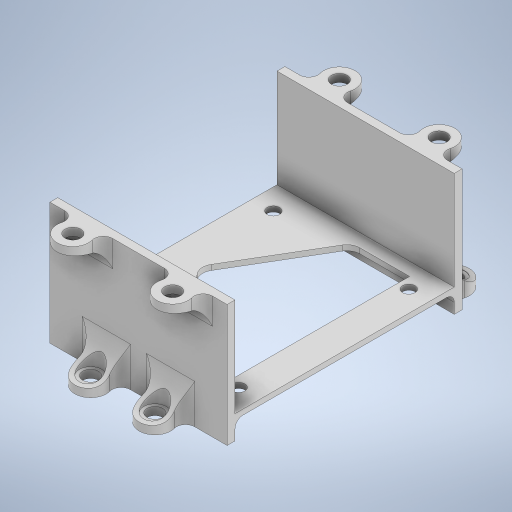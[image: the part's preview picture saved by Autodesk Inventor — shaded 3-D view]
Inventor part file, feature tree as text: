
AUTODESK INVENTOR PART (.ipt)
format: ipt  version: 2024 (Build 280153000, 153)  size: 629,248 bytes
history: native  units: in
note: dims shown in document units (in); Inventor stores cm internally (conversion verified against a paired STEP export)
features: extrude x9, sketch x3, fillet x2, plane x1, projected_geometry x1
ambient origin geometry x8: Origin, YZ Plane, XZ Plane, XY Plane, X Axis, Y Axis, Z Axis, Center Point
bodies: Solid1 (feature_tree)
feature tree (16):
  extrude  "Extrusion1"  Depth=0.1181in
  extrude  "Extrusion2"  Depth=0.1969in
  extrude  "Extrusion6"  Depth=0.4724in
  extrude  "Extrusion7"  Depth=0.4724in
  extrude  "Extrusion8"  Depth=2.6575in
  plane  "Work Plane1"
  extrude  "Extrusion9"  Depth=1.3287in
  fillet  "Fillet2"  Radius=1.6437in
  fillet  "Fillet7"  Radius=0.0787in
  extrude  "Extrusion10"  Depth=1.5551in TaperAngle=0.0deg
  extrude  "Extrusion11"  Depth=0.185in
  extrude  "Extrusion12"  Depth=0.313in
  sketch  "Sketch9"  dims[d0=3.2874in d1=0.1181in]
  sketch  "Sketch10"  dims[d2=0.1181in d4=0.1969in]
  sketch  "Sketch11"  dims[d5=0.1969in d6=0.4724in d7=0.4724in d8=2.6575in d9=1.3287in d10=1.6437in d11=0.0787in d12=0.0in d13=1.5551in d14=0.2756in d15=0.0in d16=0.0in d35=0.185in d36=0.313in d38=0.313in d40=0.1181in d41=0.0in d46=0.2362in d47=0.2362in d48=0.2362in d49=0.2362in d51=0.4724in d54=0.1378in d55=0.9646in d56=1.9291in d57=0.4823in d58=0.9646in d59=0.5906in d60=0.0in d61=0.3346in d62=0.3346in d63=0.3346in d64=0.3346in d65=0.4724in d66=0.0in d67=1.1811in d68=0.1181in d69=0.1969in d70=0.0in d72=0.3346in d73=2.5512in d74=1.2756in d75=2.7559in d76=0.0in d77=0.1969in d80=0.1181in d85=0.1181in d87=0.0662in d90=0.2362in d91=0.4724in d92=0.2756in d93=1.4961in d94=2.6575in d95=0.5807in d96=0.3937in d97=0.0in d100=0.3346in d102=0.2756in d103=0.0in d105=0.1181in d106=0.315in d107=0.315in d108=0.1181in d109=0.1476in d110=0.1476in d111=0.0in d112=0.0in d31=0.0197in d32=0.0344in d33=0.0197in d34=0.0344in]
  projected_geometry  "Projected Loop3"
